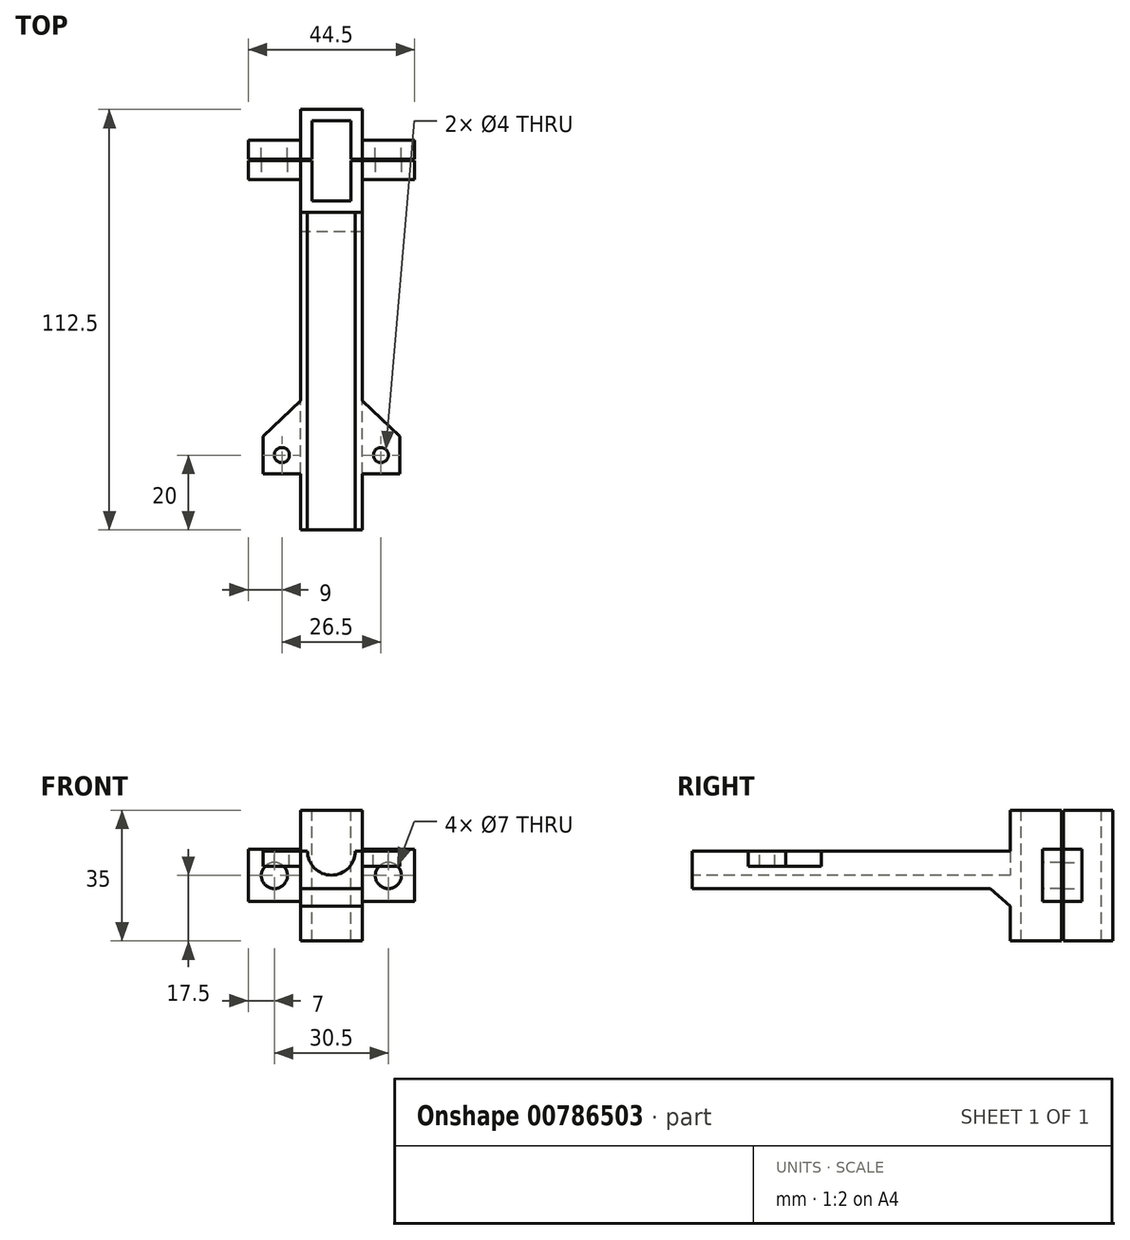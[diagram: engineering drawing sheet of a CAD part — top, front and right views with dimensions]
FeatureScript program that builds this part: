
annotation { "Feature Type Name" : "Feature", "Feature Type Description" : "" }
export const myFeature = defineFeature(function(context is Context, id is Id, definition is map)
    precondition{}
    {
        {
            var Q0;
            Q0=qCreatedBy(makeId("Top.planeOp"),FACE);
            var sketch = newSketch(context, id + "F0", { "sketchPlane" : qUnion([Q0])});
            skLineSegment(sketch, "E0.bottom", {"start": v(0, 0) * mm, "end": v(-16.5, 0) * mm});
            skLineSegment(sketch, "E0.top", {"start": v(0, -27.5) * mm, "end": v(-16.5, -27.5) * mm});
            skLineSegment(sketch, "E0.left", {"start": v(0, 0) * mm, "end": v(0, -27.5) * mm});
            skLineSegment(sketch, "E0.right", {"start": v(-16.5, 0) * mm, "end": v(-16.5, -27.5) * mm});
            skSolve(sketch);
        }
        {
            var Q0;
            Q0=qSketchRegion(id+"F0",true);
            extrude(context, id + "F1", {"entities" : qUnion([Q0]), "depth" : 35 * mm, "offsetDistance" : 25 * mm});
        }
        {
            var Q0;
            Q0=makeQuery(id+"F1.opExtrude","CAP_FACE",FACE,{"disambiguationData":[OSD([sQuery(id+"F0.wireOp",EDGE,"E0.bottom"),sQuery(id+"F0.wireOp",EDGE,"E0.top"),sQuery(id+"F0.wireOp",EDGE,"E0.left"),sQuery(id+"F0.wireOp",EDGE,"E0.right")])],"isStart":false});
            var sketch = newSketch(context, id + "F2", { "sketchPlane" : qUnion([Q0])});
            skLineSegment(sketch, "E1.bottom", {"start": v(-3, -3) * mm, "end": v(-13.5, -3) * mm});
            skLineSegment(sketch, "E1.top", {"start": v(-3, -24.5) * mm, "end": v(-13.5, -24.5) * mm});
            skLineSegment(sketch, "E1.left", {"start": v(-3, -3) * mm, "end": v(-3, -24.5) * mm});
            skLineSegment(sketch, "E1.right", {"start": v(-13.5, -3) * mm, "end": v(-13.5, -24.5) * mm});
            skSolve(sketch);
        }
        {
            var Q0;
            Q0=qSketchRegion(id+"F2",true);
            extrude(context, id + "F3", {"entities" : qUnion([Q0]), "operationType" : NewBodyOperationType.REMOVE, "oppositeDirection" : true, "depth" : 35 * mm, "offsetDistance" : 25 * mm});
        }
        {
            var Q0;
            Q0=makeQuery(id+"F1.opExtrude","CAP_FACE",FACE,{"disambiguationData":[OSD([sQuery(id+"F0.wireOp",EDGE,"E0.bottom"),sQuery(id+"F0.wireOp",EDGE,"E0.top"),sQuery(id+"F0.wireOp",EDGE,"E0.left"),sQuery(id+"F0.wireOp",EDGE,"E0.right")])],"isStart":false});
            var sketch = newSketch(context, id + "F4", { "sketchPlane" : qUnion([Q0])});
            skLineSegment(sketch, "E2.bottom", {"start": v(0, -13.75) * mm, "end": v(-3, -13.75) * mm});
            skLineSegment(sketch, "E2.top", {"start": v(0, -13.25) * mm, "end": v(-3, -13.25) * mm});
            skLineSegment(sketch, "E2.left", {"start": v(0, -13.75) * mm, "end": v(0, -13.25) * mm});
            skLineSegment(sketch, "E2.right", {"start": v(-3, -13.75) * mm, "end": v(-3, -13.25) * mm});
            skLineSegment(sketch, "E3.bottom", {"start": v(-13.5, -13.75) * mm, "end": v(-16.5, -13.75) * mm});
            skLineSegment(sketch, "E3.top", {"start": v(-13.5, -13.25) * mm, "end": v(-16.5, -13.25) * mm});
            skLineSegment(sketch, "E3.left", {"start": v(-13.5, -13.75) * mm, "end": v(-13.5, -13.25) * mm});
            skLineSegment(sketch, "E3.right", {"start": v(-16.5, -13.75) * mm, "end": v(-16.5, -13.25) * mm});
            skSolve(sketch);
        }
        {
            var Q0;
            Q0=qSketchRegion(id+"F4",true);
            extrude(context, id + "F5", {"entities" : qUnion([Q0]), "operationType" : NewBodyOperationType.REMOVE, "oppositeDirection" : true, "depth" : 35 * mm, "offsetDistance" : 25 * mm});
        }
        {
            var Q0;
            {var subQ0=sQuery(id+"F0.wireOp",EDGE,"E0.right");var subQ2=sQuery(id+"F0.wireOp",EDGE,"E0.top");Q0=makeQuery(id+"F5.boolean.opBoolean","SPLIT",FACE,{"disambiguationData":[TD([makeQuery(id+"F1.opExtrude","SWEPT_FACE",FACE,{"disambiguationData":[OSD([subQ2])]})])],"derivedFrom":makeQuery(id+"F1.opExtrude","SWEPT_FACE",FACE,{"disambiguationData":[OSD([subQ0])]})});}
            var sketch = newSketch(context, id + "F6", { "sketchPlane" : qUnion([Q0])});
            skLineSegment(sketch, "E4.bottom", {"start": v(13.75, 24.5) * mm, "end": v(18.75, 24.5) * mm});
            skLineSegment(sketch, "E4.top", {"start": v(13.75, 10.5) * mm, "end": v(18.75, 10.5) * mm});
            skLineSegment(sketch, "E4.left", {"start": v(13.75, 24.5) * mm, "end": v(13.75, 10.5) * mm});
            skLineSegment(sketch, "E4.right", {"start": v(18.75, 24.5) * mm, "end": v(18.75, 10.5) * mm});
            skSolve(sketch);
        }
        {
            var Q0;
            Q0=qSketchRegion(id+"F6",true);
            extrude(context, id + "F7", {"entities" : qUnion([Q0]), "operationType" : NewBodyOperationType.ADD, "depth" : 14 * mm, "offsetDistance" : 25 * mm});
        }
        {
            var Q0;
            Q0=makeQuery(id+"F7.opExtrude","SWEPT_FACE",FACE,{"disambiguationData":[OSD([sQuery(id+"F6.wireOp",EDGE,"E4.right")])]});
            var sketch = newSketch(context, id + "F8", { "sketchPlane" : qUnion([Q0])});
            skCircle(sketch, "E5", {"center": v(-23.5, 17.5) * mm, "radius": 3.5 * mm});
            skPoint(sketch, "E5.centerSnap0", {"position": v(-30.5, 17.5) * mm});
            skPoint(sketch, "E5.centerSnap1", {"position": v(-23.5, 24.5) * mm});
            skSolve(sketch);
        }
        {
            var Q0;
            Q0=qSketchRegion(id+"F8",true);
            extrude(context, id + "F9", {"entities" : qUnion([Q0]), "operationType" : NewBodyOperationType.REMOVE, "oppositeDirection" : true, "depth" : 5 * mm, "offsetDistance" : 25 * mm});
        }
        {
            var Q0;
            {var subQ0=sQuery(id+"F0.wireOp",EDGE,"E0.right");var subQ2=sQuery(id+"F0.wireOp",EDGE,"E0.top");Q0=makeQuery(id+"F5.boolean.opBoolean","SPLIT",FACE,{"disambiguationData":[TD([makeQuery(id+"F1.opExtrude","SWEPT_FACE",FACE,{"disambiguationData":[OSD([subQ2])]})])],"derivedFrom":makeQuery(id+"F1.opExtrude","SWEPT_FACE",FACE,{"disambiguationData":[OSD([subQ0])]})});}
            cPlane(context, id + "F10", {"entities" : qUnion([Q0]), "cplaneType" : CPlaneType.OFFSET, "offset" : 8.25 * mm, "oppositeDirection" : true, "width" : 150 * mm, "height" : 150 * mm});
        }
        {
            var Q0;
            Q0=makeQuery(id+"F5.boolean.opBoolean","SPLIT",BODY,{"disambiguationData":[OD(1.0)],"derivedFrom":makeQuery(id+"F1.opExtrude","SWEPT_BODY",BODY,{"disambiguationData":[OSD([sQuery(id+"F0.wireOp",EDGE,"E0.bottom"),sQuery(id+"F0.wireOp",EDGE,"E0.top"),sQuery(id+"F0.wireOp",EDGE,"E0.left"),sQuery(id+"F0.wireOp",EDGE,"E0.right")])]})});
            var Q1;
            Q1=qCreatedBy(id+"F10.planeOp",FACE);
            mirror(context, id + "F11", {"operationType" : NewBodyOperationType.ADD, "entities" : qUnion([Q0]), "mirrorPlane" : qUnion([Q1])});
        }
        {
            var Q0;
            {var subQ0=sQuery(id+"F0.wireOp",EDGE,"E0.bottom");var subQ1=sQuery(id+"F0.wireOp",EDGE,"E0.right");Q0=makeQuery(id+"F5.boolean.opBoolean","SPLIT",FACE,{"disambiguationData":[TD([makeQuery(id+"F1.opExtrude","SWEPT_FACE",FACE,{"disambiguationData":[OSD([subQ0])]})])],"derivedFrom":makeQuery(id+"F1.opExtrude","SWEPT_FACE",FACE,{"disambiguationData":[OSD([subQ1])]})});}
            var sketch = newSketch(context, id + "F12", { "sketchPlane" : qUnion([Q0])});
            skLineSegment(sketch, "E6.bottom", {"start": v(13.25, 24.5) * mm, "end": v(8.25, 24.5) * mm});
            skLineSegment(sketch, "E6.top", {"start": v(13.25, 10.5) * mm, "end": v(8.25, 10.5) * mm});
            skLineSegment(sketch, "E6.left", {"start": v(13.25, 24.5) * mm, "end": v(13.25, 10.5) * mm});
            skLineSegment(sketch, "E6.right", {"start": v(8.25, 24.5) * mm, "end": v(8.25, 10.5) * mm});
            skSolve(sketch);
        }
        {
            var Q0;
            Q0=qSketchRegion(id+"F12",true);
            extrude(context, id + "F13", {"entities" : qUnion([Q0]), "operationType" : NewBodyOperationType.ADD, "depth" : 14 * mm, "offsetDistance" : 25 * mm});
        }
        {
            var Q0;
            Q0=makeQuery(id+"F13.opExtrude","SWEPT_FACE",FACE,{"disambiguationData":[OSD([sQuery(id+"F12.wireOp",EDGE,"E6.right")])]});
            var sketch = newSketch(context, id + "F14", { "sketchPlane" : qUnion([Q0])});
            skCircle(sketch, "E7", {"center": v(23.5, 17.5) * mm, "radius": 3.5 * mm});
            skPoint(sketch, "E7.centerSnap0", {"position": v(16.5, 17.5) * mm});
            skPoint(sketch, "E7.centerSnap1", {"position": v(23.5, 24.5) * mm});
            skSolve(sketch);
        }
        {
            var Q0;
            Q0=qSketchRegion(id+"F14",true);
            extrude(context, id + "F15", {"entities" : qUnion([Q0]), "operationType" : NewBodyOperationType.REMOVE, "oppositeDirection" : true, "depth" : 255 * mm, "offsetDistance" : 25 * mm});
        }
        {
            var Q0;
            Q0=makeQuery(id+"F5.boolean.opBoolean","SPLIT",BODY,{"disambiguationData":[OD(0.0)],"derivedFrom":makeQuery(id+"F1.opExtrude","SWEPT_BODY",BODY,{"disambiguationData":[OSD([sQuery(id+"F0.wireOp",EDGE,"E0.bottom"),sQuery(id+"F0.wireOp",EDGE,"E0.top"),sQuery(id+"F0.wireOp",EDGE,"E0.left"),sQuery(id+"F0.wireOp",EDGE,"E0.right")])]})});
            var Q1;
            Q1=qCreatedBy(id+"F10.planeOp",FACE);
            mirror(context, id + "F16", {"operationType" : NewBodyOperationType.ADD, "entities" : qUnion([Q0]), "mirrorPlane" : qUnion([Q1])});
        }
        {
            var Q0;
            Q0=makeQuery(id+"F1.opExtrude","SWEPT_FACE",FACE,{"disambiguationData":[OSD([sQuery(id+"F0.wireOp",EDGE,"E0.top")])]});
            var sketch = newSketch(context, id + "F17", { "sketchPlane" : qUnion([Q0])});
            skLineSegment(sketch, "E8.bottom", {"start": v(-16.5, 28) * mm, "end": v(0, 28) * mm});
            skLineSegment(sketch, "E8.top", {"start": v(-16.5, 14) * mm, "end": v(0, 14) * mm});
            skLineSegment(sketch, "E8.left", {"start": v(-16.5, 28) * mm, "end": v(-16.5, 14) * mm});
            skLineSegment(sketch, "E8.right", {"start": v(0, 28) * mm, "end": v(0, 14) * mm});
            skSolve(sketch);
        }
        {
            var Q0;
            Q0 = qSketchRegion(id + "F17", true);
            extrude(context, id + "F18", {"entities" : qUnion([Q0]), "operationType" : NewBodyOperationType.ADD, "depth" : 85 * mm, "offsetDistance" : 25 * mm});
        }
        {
            var Q0;
            Q0=makeQuery(id+"F18.opExtrude","CAP_FACE",FACE,{"disambiguationData":[OSD([sQuery(id+"F17.wireOp",EDGE,"E8.bottom"),sQuery(id+"F17.wireOp",EDGE,"E8.top"),sQuery(id+"F17.wireOp",EDGE,"E8.left"),sQuery(id+"F17.wireOp",EDGE,"E8.right")])],"isStart":false});
            var sketch = newSketch(context, id + "F19", { "sketchPlane" : qUnion([Q0])});
            skArc(sketch, "E9", {"start": v(-14.65, 24) * mm, "mid": v(-8.25, 17.6) * mm, "end": v(-1.85, 24) * mm});
            skPoint(sketch, "E9.centerSnap0", {"position": v(0, 21) * mm});
            skPoint(sketch, "E9.centerSnap1", {"position": v(-8.25, 14) * mm});
            skLineSegment(sketch, "E10", {"start": v(-14.65, 24) * mm, "end": v(-16.5, 24) * mm});
            skLineSegment(sketch, "E11", {"start": v(-1.85, 24) * mm, "end": v(0, 24) * mm});
            skLineSegment(sketch, "E12", {"start": v(-16.5, 24) * mm, "end": v(-16.5, 28) * mm});
            skLineSegment(sketch, "E13", {"start": v(-16.5, 28) * mm, "end": v(0, 28) * mm});
            skLineSegment(sketch, "E14", {"start": v(0, 28) * mm, "end": v(0, 24) * mm});
            skSolve(sketch);
        }
        {
            var Q0;
            Q0 = qSketchRegion(id + "F19", true);
            extrude(context, id + "F20", {"entities" : qUnion([Q0]), "operationType" : NewBodyOperationType.REMOVE, "oppositeDirection" : true, "depth" : 85 * mm, "offsetDistance" : 25 * mm});
        }
        {
            var Q0;
            {var subQ0=sQuery(id+"F0.wireOp",EDGE,"E0.right");var subQ2=sQuery(id+"F0.wireOp",EDGE,"E0.top");Q0=makeQuery(id+"F18.boolean.opBoolean","MERGE",FACE,{"derivedFrom":[makeQuery(id+"F5.boolean.opBoolean","SPLIT",FACE,{"disambiguationData":[TD([makeQuery(id+"F1.opExtrude","SWEPT_FACE",FACE,{"disambiguationData":[OSD([subQ2])]})])],"derivedFrom":makeQuery(id+"F1.opExtrude","SWEPT_FACE",FACE,{"disambiguationData":[OSD([subQ0])]})}),makeQuery(id+"F18.opExtrude","SWEPT_FACE",FACE,{"disambiguationData":[OSD([sQuery(id+"F17.wireOp",EDGE,"E8.left")])]})]});}
            var sketch = newSketch(context, id + "F21", { "sketchPlane" : qUnion([Q0])});
            skLineSegment(sketch, "E15.bottom", {"start": v(97.5, 24) * mm, "end": v(87.5, 24) * mm});
            skLineSegment(sketch, "E15.top", {"start": v(97.5, 20) * mm, "end": v(87.5, 20) * mm});
            skLineSegment(sketch, "E15.left", {"start": v(97.5, 24) * mm, "end": v(97.5, 20) * mm});
            skLineSegment(sketch, "E15.right", {"start": v(87.5, 24) * mm, "end": v(87.5, 20) * mm});
            skSolve(sketch);
        }
        {
            var Q0;
            Q0 = qSketchRegion(id + "F21", true);
            extrude(context, id + "F22", {"entities" : qUnion([Q0]), "operationType" : NewBodyOperationType.ADD, "depth" : 10 * mm, "offsetDistance" : 25 * mm});
        }
        {
            var Q0;
            Q0=makeQuery(id+"F22.boolean.opBoolean","MERGE",FACE,{"derivedFrom":[makeQuery(id+"F20.boolean.opBoolean","COPY",FACE,{"derivedFrom":makeQuery(id+"F20.opExtrude","SWEPT_FACE",FACE,{"disambiguationData":[OSD([sQuery(id+"F19.wireOp",EDGE,"E10")])]})}),makeQuery(id+"F22.opExtrude","SWEPT_FACE",FACE,{"disambiguationData":[OSD([sQuery(id+"F21.wireOp",EDGE,"E15.bottom")])]})]});
            var sketch = newSketch(context, id + "F23", { "sketchPlane" : qUnion([Q0])});
            skLineSegment(sketch, "E16", {"start": v(-26.5, -87.5) * mm, "end": v(-16.5, -77.97) * mm});
            skLineSegment(sketch, "E17", {"start": v(-16.5, -77.97) * mm, "end": v(-16.5, -87.5) * mm});
            skLineSegment(sketch, "E18", {"start": v(-16.5, -87.5) * mm, "end": v(-26.5, -87.5) * mm});
            skSolve(sketch);
        }
        {
            var Q0;
            Q0 = qSketchRegion(id + "F23", true);
            extrude(context, id + "F24", {"entities" : qUnion([Q0]), "operationType" : NewBodyOperationType.ADD, "oppositeDirection" : true, "depth" : 4 * mm, "offsetDistance" : 25 * mm});
        }
        {
            var Q0;
            Q0=makeQuery(id+"F24.boolean.opBoolean","MERGE",FACE,{"derivedFrom":[makeQuery(id+"F22.boolean.opBoolean","MERGE",FACE,{"derivedFrom":[makeQuery(id+"F20.boolean.opBoolean","COPY",FACE,{"derivedFrom":makeQuery(id+"F20.opExtrude","SWEPT_FACE",FACE,{"disambiguationData":[OSD([sQuery(id+"F19.wireOp",EDGE,"E10")])]})}),makeQuery(id+"F22.opExtrude","SWEPT_FACE",FACE,{"disambiguationData":[OSD([sQuery(id+"F21.wireOp",EDGE,"E15.bottom")])]})]}),makeQuery(id+"F24.opExtrude","CAP_FACE",FACE,{"disambiguationData":[OSD([sQuery(id+"F23.wireOp",EDGE,"E16"),sQuery(id+"F23.wireOp",EDGE,"E17"),sQuery(id+"F23.wireOp",EDGE,"E18")])],"isStart":true})]});
            var sketch = newSketch(context, id + "F25", { "sketchPlane" : qUnion([Q0])});
            skCircle(sketch, "E19", {"center": v(-21.5, -92.5) * mm, "radius": 2 * mm});
            skPoint(sketch, "E19.centerSnap0", {"position": v(-21.5, -97.5) * mm});
            skPoint(sketch, "E19.centerSnap1", {"position": v(-26.5, -92.5) * mm});
            skSolve(sketch);
        }
        {
            var Q0;
            Q0 = qSketchRegion(id + "F25", true);
            extrude(context, id + "F26", {"entities" : qUnion([Q0]), "operationType" : NewBodyOperationType.REMOVE, "oppositeDirection" : true, "depth" : 4 * mm, "offsetDistance" : 25 * mm});
        }
        {
            var Q0;
            Q0=makeQuery(id+"F5.boolean.opBoolean","SPLIT",BODY,{"disambiguationData":[OD(1.0)],"derivedFrom":makeQuery(id+"F1.opExtrude","SWEPT_BODY",BODY,{"disambiguationData":[OSD([sQuery(id+"F0.wireOp",EDGE,"E0.bottom"),sQuery(id+"F0.wireOp",EDGE,"E0.top"),sQuery(id+"F0.wireOp",EDGE,"E0.left"),sQuery(id+"F0.wireOp",EDGE,"E0.right")])]})});
            var Q1;
            Q1=qCreatedBy(id+"F10.planeOp",FACE);
            mirror(context, id + "F27", {"operationType" : NewBodyOperationType.ADD, "entities" : qUnion([Q0]), "mirrorPlane" : qUnion([Q1])});
        }
        {
            var Q0;
            {var subQ0=sQuery(id+"F0.wireOp",EDGE,"E0.right");var subQ2=sQuery(id+"F0.wireOp",EDGE,"E0.top");Q0=makeQuery(id+"F18.boolean.opBoolean","MERGE",FACE,{"derivedFrom":[makeQuery(id+"F5.boolean.opBoolean","SPLIT",FACE,{"disambiguationData":[TD([makeQuery(id+"F1.opExtrude","SWEPT_FACE",FACE,{"disambiguationData":[OSD([subQ2])]})])],"derivedFrom":makeQuery(id+"F1.opExtrude","SWEPT_FACE",FACE,{"disambiguationData":[OSD([subQ0])]})}),makeQuery(id+"F18.opExtrude","SWEPT_FACE",FACE,{"disambiguationData":[OSD([sQuery(id+"F17.wireOp",EDGE,"E8.left")])]})]});}
            var sketch = newSketch(context, id + "F28", { "sketchPlane" : qUnion([Q0])});
            skLineSegment(sketch, "E20", {"start": v(27.5, 9.25) * mm, "end": v(32.75, 14) * mm});
            skLineSegment(sketch, "E21", {"start": v(32.75, 14) * mm, "end": v(27.5, 14) * mm});
            skLineSegment(sketch, "E22", {"start": v(27.5, 14) * mm, "end": v(27.5, 9.25) * mm});
            skLineSegment(sketch, "E23", {"start": v(27.5, 29.5) * mm, "end": v(32.75, 24) * mm});
            skLineSegment(sketch, "E24", {"start": v(32.75, 24) * mm, "end": v(27.5, 24) * mm});
            skLineSegment(sketch, "E25", {"start": v(27.5, 24) * mm, "end": v(27.5, 29.5) * mm});
            skSolve(sketch);
        }
        {
            var Q0;
            Q0=makeQuery(id+"F28.imprint","IMPRINT",FACE,{"disambiguationData":[TD([[makeQuery(id+"F28.imprint","IMPRINT",EDGE,{"derivedFrom":sQuery(id+"F28.wireOp",EDGE,"E20")}),1.0]])]});
            extrude(context, id + "F29", {"entities" : qUnion([Q0]), "operationType" : NewBodyOperationType.ADD, "oppositeDirection" : true, "depth" : 16.5 * mm, "offsetDistance" : 25 * mm});
        }
    });
